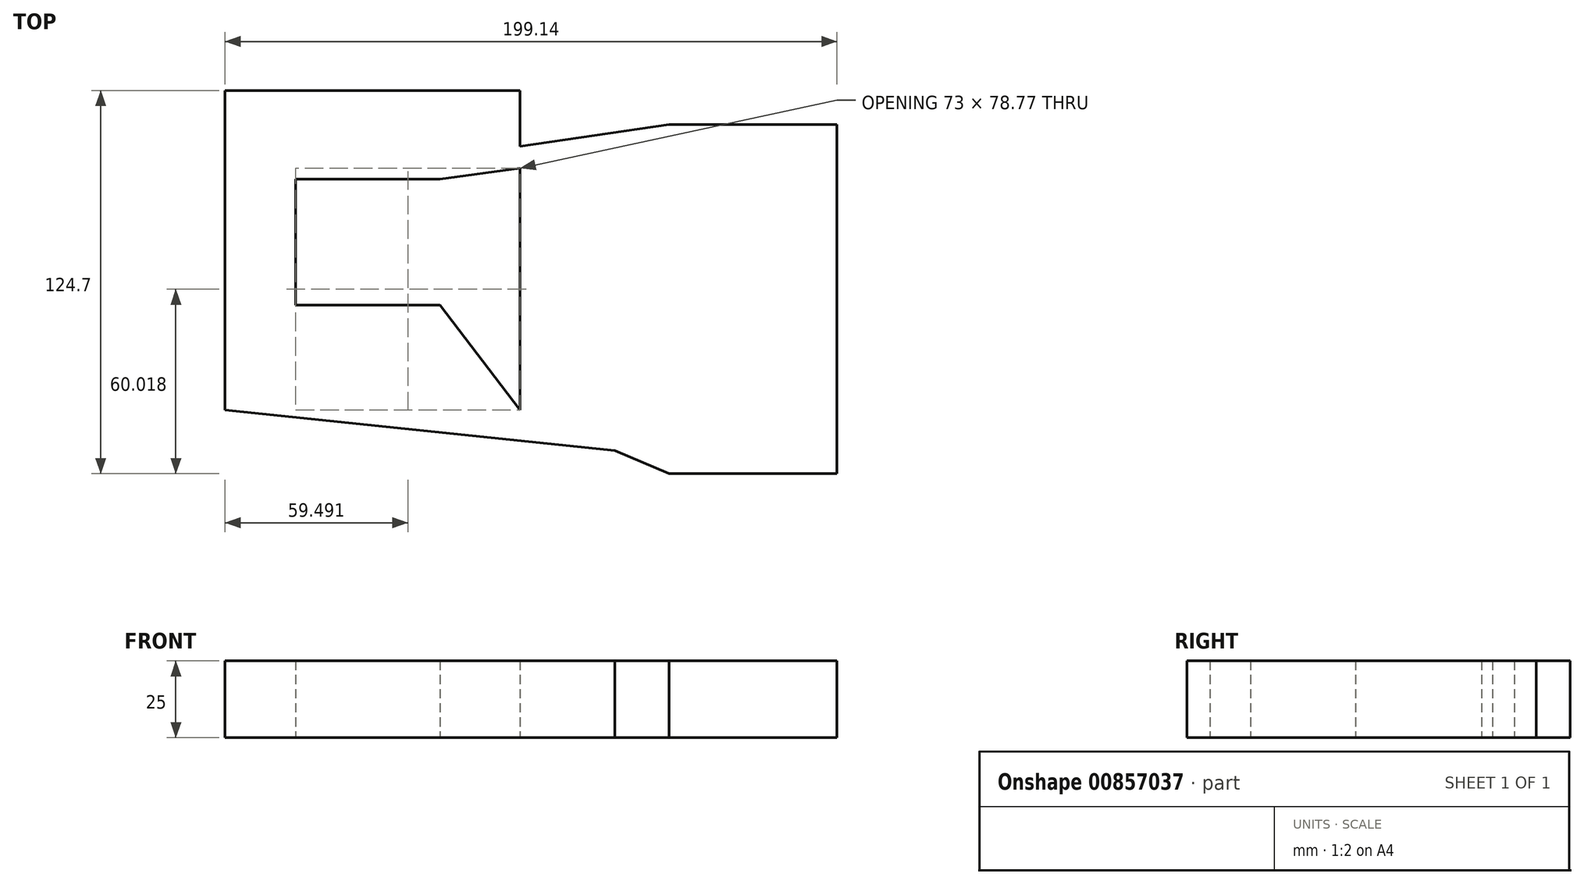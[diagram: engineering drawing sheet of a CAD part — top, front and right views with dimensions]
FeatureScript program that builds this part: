
annotation { "Feature Type Name" : "Feature", "Feature Type Description" : "" }
export const myFeature = defineFeature(function(context is Context, id is Id, definition is map)
    precondition{}
    {
        {
            var Q0;
            Q0=qCreatedBy(makeId("Top.planeOp"),FACE);
            var sketch = newSketch(context, id + "F0", { "sketchPlane" : qUnion([Q0])});
            skLineSegment(sketch, "E0", {"start": v(-37.74, 48.77) * mm, "end": v(51.41, 48.77) * mm});
            skLineSegment(sketch, "E1", {"start": v(51.41, 48.77) * mm, "end": v(51.41, -55.3) * mm});
            skLineSegment(sketch, "E2", {"start": v(51.41, -55.3) * mm, "end": v(-44.58, -55.3) * mm});
            skLineSegment(sketch, "E3", {"start": v(-44.58, -55.3) * mm, "end": v(-44.58, 48.77) * mm});
            skLineSegment(sketch, "E4", {"start": v(-44.58, 48.77) * mm, "end": v(-37.74, 48.77) * mm});
            skLineSegment(sketch, "E5.bottom", {"start": v(-21.6, 19.88) * mm, "end": v(25.32, 19.88) * mm});
            skLineSegment(sketch, "E5.top", {"start": v(-21.6, -21.12) * mm, "end": v(25.32, -21.12) * mm});
            skLineSegment(sketch, "E5.left", {"start": v(-21.6, 19.88) * mm, "end": v(-21.6, -21.12) * mm});
            skLineSegment(sketch, "E5.right", {"start": v(25.32, 19.88) * mm, "end": v(25.32, -21.12) * mm});
            skLineSegment(sketch, "E6.bottom", {"start": v(154.56, 37.67) * mm, "end": v(99.86, 37.67) * mm});
            skLineSegment(sketch, "E6.top", {"start": v(154.56, -75.93) * mm, "end": v(99.86, -75.93) * mm});
            skLineSegment(sketch, "E6.left", {"start": v(154.56, 37.67) * mm, "end": v(154.56, -75.93) * mm});
            skLineSegment(sketch, "E6.right", {"start": v(99.86, 37.67) * mm, "end": v(99.86, -75.93) * mm});
            skLineSegment(sketch, "E7", {"start": v(154.56, 37.67) * mm, "end": v(25.32, 19.88) * mm});
            skLineSegment(sketch, "E8", {"start": v(99.86, 37.67) * mm, "end": v(-21.6, 19.88) * mm});
            skLineSegment(sketch, "E9", {"start": v(154.56, -75.93) * mm, "end": v(-44.58, -55.3) * mm});
            skLineSegment(sketch, "E10", {"start": v(99.86, -75.93) * mm, "end": v(51.41, -55.3) * mm});
            skLineSegment(sketch, "E11", {"start": v(51.41, -55.3) * mm, "end": v(25.32, -21.12) * mm});
            skLineSegment(sketch, "E12", {"start": v(-44.58, -55.3) * mm, "end": v(-21.6, -21.12) * mm});
            skSolve(sketch);
        }
        {
            var Q0;
            Q0 = qSketchRegion(id + "F0", true);
            extrude(context, id + "F1", {"entities" : qUnion([Q0]), "depth" : 25 * mm, "offsetDistance" : 25 * mm});
        }
    });
